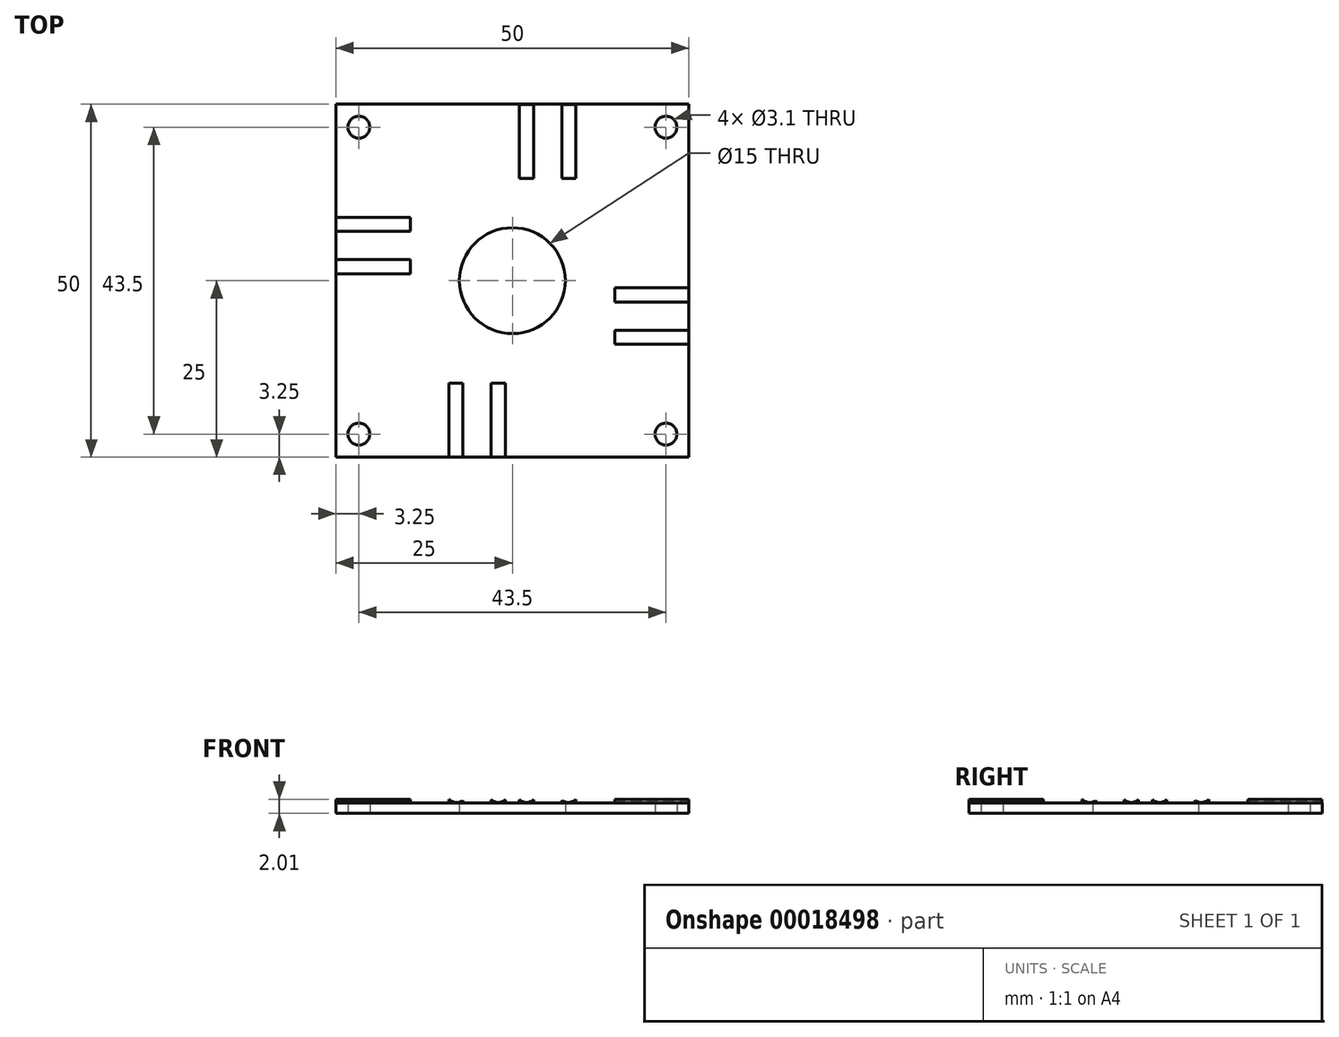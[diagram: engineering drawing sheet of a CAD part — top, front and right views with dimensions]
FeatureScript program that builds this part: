
annotation { "Feature Type Name" : "Feature", "Feature Type Description" : "" }
export const myFeature = defineFeature(function(context is Context, id is Id, definition is map)
    precondition{}
    {
        {
            var Q0;
            Q0=qCreatedBy(makeId("Top.planeOp"),FACE);
            var sketch = newSketch(context, id + "F0", { "sketchPlane" : qUnion([Q0])});
            skLineSegment(sketch, "E0.rect.bottom", {"start": v(-25, 25) * mm, "end": v(25, 25) * mm});
            skLineSegment(sketch, "E0.rect.top", {"start": v(-25, -25) * mm, "end": v(25, -25) * mm});
            skLineSegment(sketch, "E0.rect.left", {"start": v(-25, 25) * mm, "end": v(-25, -25) * mm});
            skLineSegment(sketch, "E0.rect.right", {"start": v(25, 25) * mm, "end": v(25, -25) * mm});
            skPoint(sketch, "E0.rect.middle", {"position": v(0, 0) * mm});
            skLineSegment(sketch, "E1", {"start": v(-25, 25) * mm, "end": v(25, -25) * mm, "construction": true});
            skLineSegment(sketch, "E2", {"start": v(25, 25) * mm, "end": v(-25, -25) * mm, "construction": true});
            skLineSegment(sketch, "E3", {"start": v(0, -25) * mm, "end": v(0, 25) * mm, "construction": true});
            skLineSegment(sketch, "E4", {"start": v(-25, 0) * mm, "end": v(25, 0) * mm, "construction": true});
            skCircle(sketch, "E5", {"center": v(0, 0) * mm, "radius": 7.5 * mm});
            skCircle(sketch, "E6", {"center": v(-21.75, 21.75) * mm, "radius": 1.55 * mm});
            skCircle(sketch, "E7.1.0", {"center": v(-21.75, -21.75) * mm, "radius": 1.55 * mm});
            skCircle(sketch, "E7.2.0", {"center": v(21.75, -21.75) * mm, "radius": 1.55 * mm});
            skCircle(sketch, "E7.3.0", {"center": v(21.75, 21.75) * mm, "radius": 1.55 * mm});
            skSolve(sketch);
        }
        {
            var Q0;
            Q0 = qSketchRegion(id + "F0", true);
            extrude(context, id + "F1", {"entities" : qUnion([Q0]), "depth" : 1.5 * mm});
        }
        {
            var Q0;
            Q0=makeQuery(id+"F1.opExtrude","SWEPT_FACE",FACE,{"disambiguationData":[OSD([sQuery(id+"F0.wireOp",EDGE,"E0.rect.top")])]});
            var sketch = newSketch(context, id + "F2", { "sketchPlane" : qUnion([Q0])});
            skLineSegment(sketch, "E8.bottom", {"start": v(-3, 1.5) * mm, "end": v(-1, 1.5) * mm});
            skLineSegment(sketch, "E8.top", {"start": v(-3, 3.1) * mm, "end": v(-1, 3.1) * mm});
            skLineSegment(sketch, "E8.left", {"start": v(-3, 1.5) * mm, "end": v(-3, 3.1) * mm});
            skLineSegment(sketch, "E8.right", {"start": v(-1, 1.5) * mm, "end": v(-1, 3.1) * mm});
            skLineSegment(sketch, "E9.bottom", {"start": v(-9, 1.5) * mm, "end": v(-7, 1.5) * mm});
            skLineSegment(sketch, "E9.top", {"start": v(-9, 3.1) * mm, "end": v(-7, 3.1) * mm});
            skLineSegment(sketch, "E9.left", {"start": v(-9, 1.5) * mm, "end": v(-9, 3.1) * mm});
            skLineSegment(sketch, "E9.right", {"start": v(-7, 1.5) * mm, "end": v(-7, 3.1) * mm});
            skSolve(sketch);
        }
        {
            var Q0;
            Q0=makeQuery(id+"F2.imprint","IMPRINT",FACE,{"disambiguationData":[TD([[makeQuery(id+"F2.imprint","IMPRINT",EDGE,{"derivedFrom":sQuery(id+"F2.wireOp",EDGE,"E9.bottom")}),1.0]])]});
            var Q1;
            Q1=makeQuery(id+"F2.imprint","IMPRINT",FACE,{"disambiguationData":[TD([[makeQuery(id+"F2.imprint","IMPRINT",EDGE,{"derivedFrom":sQuery(id+"F2.wireOp",EDGE,"E8.bottom")}),1.0]])]});
            extrude(context, id + "F3", {"entities" : qUnion([Q0, Q1]), "oppositeDirection" : true, "depth" : 18 * mm - 7.5 * mm});
        }
        {
            var Q0;
            Q0=makeQuery(id+"F3.opExtrude","CAP_FACE",FACE,{"disambiguationData":[OSD([sQuery(id+"F2.wireOp",EDGE,"E8.bottom"),sQuery(id+"F2.wireOp",EDGE,"E8.top"),sQuery(id+"F2.wireOp",EDGE,"E8.left"),sQuery(id+"F2.wireOp",EDGE,"E8.right")])],"isStart":true});
            var sketch = newSketch(context, id + "F4", { "sketchPlane" : qUnion([Q0])});
            skCircle(sketch, "E10", {"center": v(-2, 3.1) * mm, "radius": 1.55 * mm});
            skCircle(sketch, "E11", {"center": v(-7.9, 3.1) * mm, "radius": 1.55 * mm});
            skSolve(sketch);
        }
        {
            var Q0;
            Q0=makeQuery(id+"F4.imprint","IMPRINT",FACE,{"disambiguationData":[TD([[makeQuery(id+"F4.imprint","IMPRINT",EDGE,{"derivedFrom":sQuery(id+"F4.wireOp",EDGE,"E11")}),1.0]])]});
            var Q1;
            {var subQ3=makeQuery(id+"F3.opExtrude","CAP_EDGE",EDGE,{"disambiguationData":[OSD([sQuery(id+"F2.wireOp",EDGE,"E8.top")])],"isStart":true});Q1=makeQuery(id+"F4.imprint","IMPRINT",FACE,{"disambiguationData":[TD([[makeQuery(id+"F4.imprint","IMPRINT",EDGE,{"derivedFrom":subQ3}),1.0]])]});}
            var Q2;
            {var subQ3=makeQuery(id+"F3.opExtrude","CAP_EDGE",EDGE,{"disambiguationData":[OSD([sQuery(id+"F2.wireOp",EDGE,"E8.top")])],"isStart":true});Q2=makeQuery(id+"F4.imprint","IMPRINT",FACE,{"disambiguationData":[TD([[makeQuery(id+"F4.imprint","IMPRINT",EDGE,{"derivedFrom":subQ3}),-1.0]])]});}
            extrude(context, id + "F5", {"entities" : qUnion([Q0, Q1, Q2]), "operationType" : NewBodyOperationType.REMOVE, "oppositeDirection" : true, "depth" : 25 * mm});
        }
        {
            var Q0;
            {var subQ3=makeQuery(id+"F3.opExtrude","CAP_EDGE",EDGE,{"disambiguationData":[OSD([sQuery(id+"F2.wireOp",EDGE,"E8.top")])],"isStart":true});Q0=makeQuery(id+"F4.imprint","IMPRINT",FACE,{"disambiguationData":[TD([[makeQuery(id+"F4.imprint","IMPRINT",EDGE,{"derivedFrom":subQ3}),1.0]])]});}
            var Q1;
            {var subQ3=makeQuery(id+"F3.opExtrude","CAP_EDGE",EDGE,{"disambiguationData":[OSD([sQuery(id+"F2.wireOp",EDGE,"E8.top")])],"isStart":true});Q1=makeQuery(id+"F4.imprint","IMPRINT",FACE,{"disambiguationData":[TD([[makeQuery(id+"F4.imprint","IMPRINT",EDGE,{"derivedFrom":subQ3}),-1.0]])]});}
            extrude(context, id + "F6", {"entities" : qUnion([Q0, Q1]), "operationType" : NewBodyOperationType.REMOVE, "oppositeDirection" : true, "depth" : 25 * mm});
        }
        {
            var Q0;
            Q0=makeQuery(id+"F1.opExtrude","CAP_FACE",FACE,{"disambiguationData":[OSD([sQuery(id+"F0.wireOp",EDGE,"E0.rect.bottom"),sQuery(id+"F0.wireOp",EDGE,"E0.rect.top"),sQuery(id+"F0.wireOp",EDGE,"E0.rect.left"),sQuery(id+"F0.wireOp",EDGE,"E0.rect.right"),sQuery(id+"F0.wireOp",EDGE,"E5"),sQuery(id+"F0.wireOp",EDGE,"E6"),sQuery(id+"F0.wireOp",EDGE,"E7.1.0"),sQuery(id+"F0.wireOp",EDGE,"E7.2.0"),sQuery(id+"F0.wireOp",EDGE,"E7.3.0")])],"isStart":false});
            var sketch = newSketch(context, id + "F7", { "sketchPlane" : qUnion([Q0])});
            skCircle(sketch, "E12", {"center": v(0, -0.02) * mm, "radius": 0.05 * mm});
            skSolve(sketch);
        }
        {
            var Q0;
            Q0 = qSketchRegion(id + "F7", true);
            extrude(context, id + "F8", {"entities" : qUnion([Q0]), "depth" : 5 * mm});
        }
        {
            var Q0;
            Q0=makeQuery(id+"F3.opExtrude","SWEPT_BODY",BODY,{"disambiguationData":[OSD([sQuery(id+"F2.wireOp",EDGE,"E8.bottom"),sQuery(id+"F2.wireOp",EDGE,"E8.top"),sQuery(id+"F2.wireOp",EDGE,"E8.left"),sQuery(id+"F2.wireOp",EDGE,"E8.right")])]});
            var Q1;
            Q1=makeQuery(id+"F3.opExtrude","SWEPT_BODY",BODY,{"disambiguationData":[OSD([sQuery(id+"F2.wireOp",EDGE,"E9.bottom"),sQuery(id+"F2.wireOp",EDGE,"E9.top"),sQuery(id+"F2.wireOp",EDGE,"E9.left"),sQuery(id+"F2.wireOp",EDGE,"E9.right")])]});
            var Q2;
            Q2=makeQuery(id+"F8.opExtrude","SWEPT_FACE",FACE,{"disambiguationData":[OSD([sQuery(id+"F7.wireOp",EDGE,"E12")])]});
            circularPattern(context, id + "F9", {"entities" : qUnion([Q0, Q1]), "axis" : qUnion([Q2]), "angle" : 90 * degree, "instanceCount" : 4});
        }
        {
            var Q0;
            Q0=makeQuery(id+"F8.opExtrude","SWEPT_BODY",BODY,{"disambiguationData":[OSD([sQuery(id+"F7.wireOp",EDGE,"E12")])]});
            deleteBodies(context, id + "F10", {"entities" : qUnion([Q0])});
        }
    });
